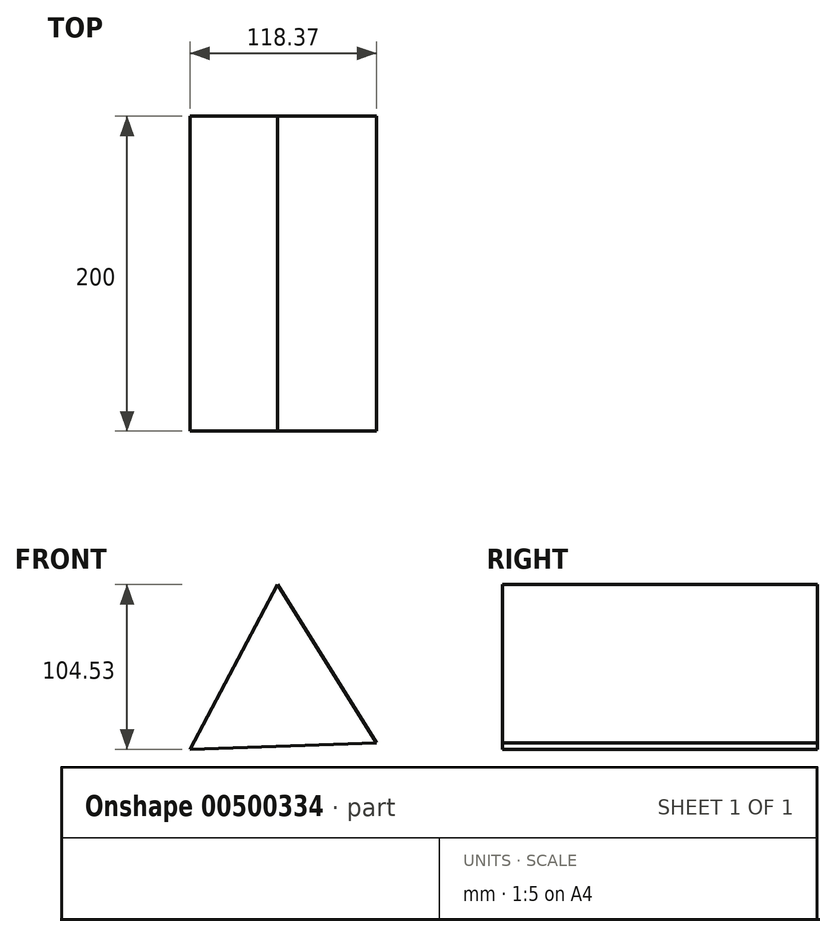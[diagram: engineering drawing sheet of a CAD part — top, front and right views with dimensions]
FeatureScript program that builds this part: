
annotation { "Feature Type Name" : "Feature", "Feature Type Description" : "" }
export const myFeature = defineFeature(function(context is Context, id is Id, definition is map)
    precondition{}
    {
        {
            var Q0;
            Q0=qCreatedBy(makeId("Front.planeOp"),FACE);
            var sketch = newSketch(context, id + "F0", { "sketchPlane" : qUnion([Q0])});
            skCircle(sketch, "E0.cCircle", {"center": v(0, 0) * mm, "radius": 68.38 * mm, "construction": true});
            skLineSegment(sketch, "E0.0", {"start": v(60.35, -32.16) * mm, "end": v(-58.02, -36.19) * mm});
            skLineSegment(sketch, "E0.1", {"start": v(-58.02, -36.19) * mm, "end": v(-2.33, 68.34) * mm});
            skLineSegment(sketch, "E0.2", {"start": v(-2.33, 68.34) * mm, "end": v(60.35, -32.16) * mm});
            skSolve(sketch);
        }
        {
            var Q0;
            Q0=makeQuery(id+"F0.imprint","IMPRINT",FACE,{"disambiguationData":[TD([[makeQuery(id+"F0.imprint","IMPRINT",EDGE,{"derivedFrom":sQuery(id+"F0.wireOp",EDGE,"E0.0")}),-1.0]])]});
            extrude(context, id + "F1", {"entities" : qUnion([Q0]), "oppositeDirection" : true, "depth" : 200 * mm});
        }
    });
